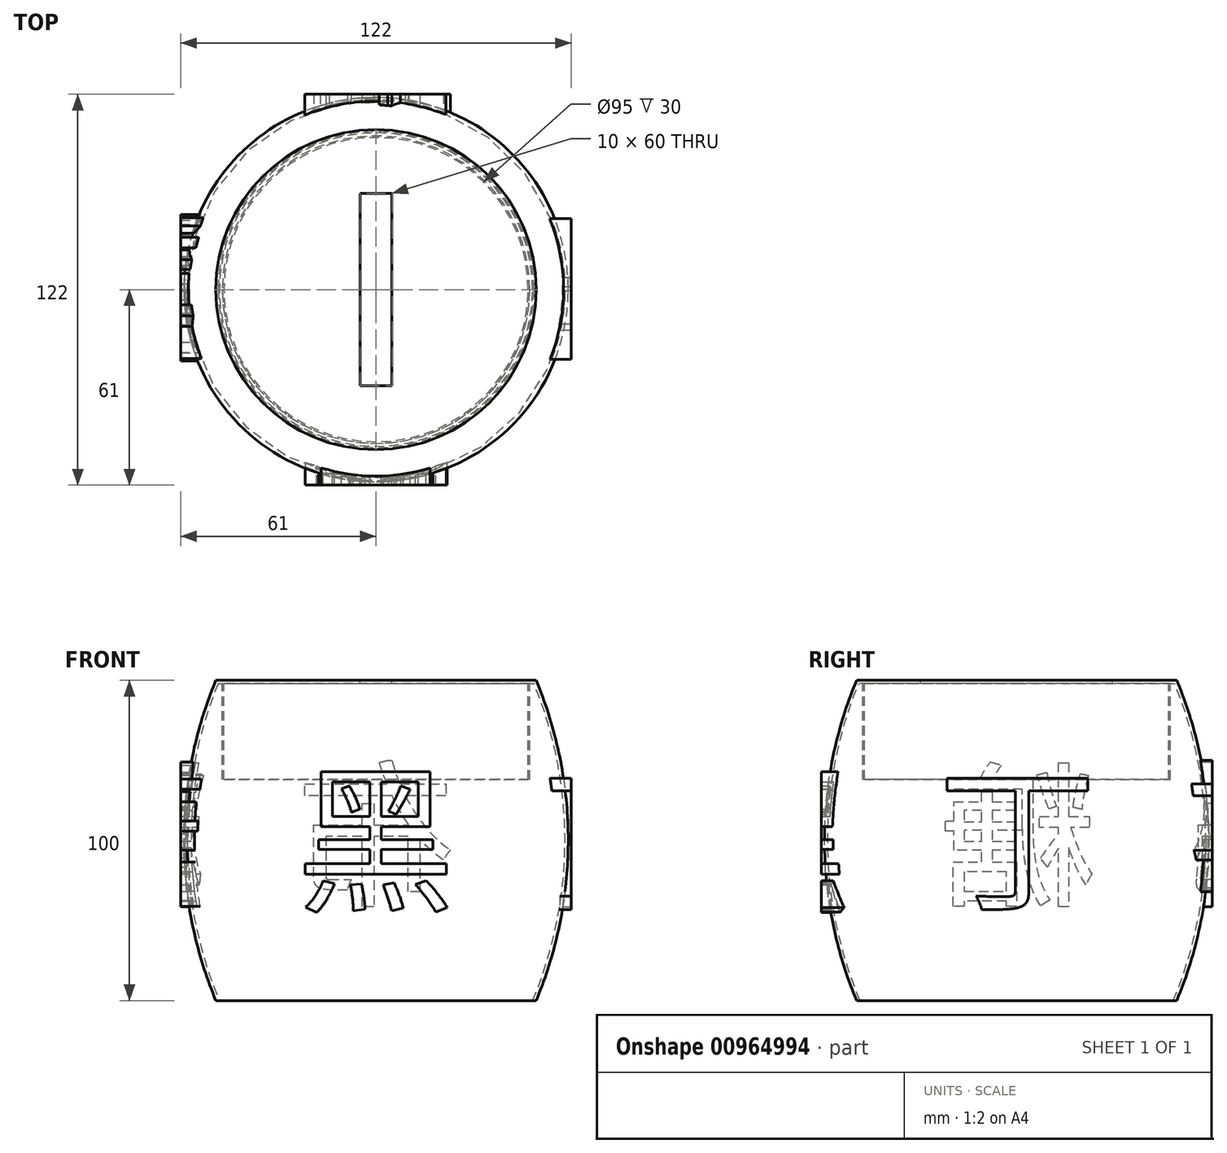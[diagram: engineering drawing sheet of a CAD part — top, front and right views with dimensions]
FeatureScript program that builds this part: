
annotation { "Feature Type Name" : "Feature", "Feature Type Description" : "" }
export const myFeature = defineFeature(function(context is Context, id is Id, definition is map)
    precondition{}
    {
        {
            var Q0;
            Q0=qCreatedBy(makeId("Front.planeOp"),FACE);
            var sketch = newSketch(context, id + "F0", { "sketchPlane" : qUnion([Q0])});
            skLineSegment(sketch, "E0.bottom", {"start": v(25, -25) * mm, "end": v(-25, -25) * mm});
            skLineSegment(sketch, "E0.top", {"start": v(25, 25) * mm, "end": v(-25, 25) * mm});
            skLineSegment(sketch, "E0.left", {"start": v(25, -25) * mm, "end": v(25, 25) * mm});
            skLineSegment(sketch, "E0.right", {"start": v(-25, -25) * mm, "end": v(-25, 25) * mm});
            skPoint(sketch, "E0.middle", {"position": v(0, 0) * mm});
            skText(sketch, "E1", { "text": "黑", "fontName": "NotoSansCJKsc-Regular.otf"});
            const initialGuessF0  = {"E1": [-0.025, -0.01845, 1, 0, 0.0359]};
            skSetInitialGuess(sketch, initialGuessF0);
            skSolve(sketch);
        }
        {
            var Q0;
            Q0=qCreatedBy(makeId("Right.planeOp"),FACE);
            var sketch = newSketch(context, id + "F1", { "sketchPlane" : qUnion([Q0])});
            skLineSegment(sketch, "E2.bottom", {"start": v(25, -25) * mm, "end": v(-25, -25) * mm});
            skLineSegment(sketch, "E2.top", {"start": v(25, 25) * mm, "end": v(-25, 25) * mm});
            skLineSegment(sketch, "E2.left", {"start": v(25, -25) * mm, "end": v(25, 25) * mm});
            skLineSegment(sketch, "E2.right", {"start": v(-25, -25) * mm, "end": v(-25, 25) * mm});
            skPoint(sketch, "E2.middle", {"position": v(0, 0) * mm});
            skText(sketch, "E3", { "text": "丁", "fontName": "NotoSansCJKsc-Regular.otf"});
            const initialGuessF1  = {"E3": [-0.025, -0.01819, 1, 0, 0.0363]};
            skSetInitialGuess(sketch, initialGuessF1);
            skSolve(sketch);
        }
        {
            var Q0;
            Q0=qCreatedBy(makeId("Right.planeOp"),FACE);
            var sketch = newSketch(context, id + "F2", { "sketchPlane" : qUnion([Q0])});
            skLineSegment(sketch, "E4.bottom", {"start": v(-25, -25) * mm, "end": v(25, -25) * mm});
            skLineSegment(sketch, "E4.top", {"start": v(-25, 25) * mm, "end": v(25, 25) * mm});
            skLineSegment(sketch, "E4.left", {"start": v(-25, -25) * mm, "end": v(-25, 25) * mm});
            skLineSegment(sketch, "E4.right", {"start": v(25, -25) * mm, "end": v(25, 25) * mm});
            skPoint(sketch, "E4.middle", {"position": v(0, 0) * mm});
            skSolve(sketch);
        }
        {
            var Q0;
            Q0 = qSketchRegion(id + "F2", true);
            extrude(context, id + "F3", {"entities" : qUnion([Q0]), "depth" : -1 * mm, "offsetDistance" : 25 * mm});
        }
        {
            var Q0;
            Q0=makeQuery(id+"F3.opExtrude","CAP_FACE",FACE,{"disambiguationData":[OSD([sQuery(id+"F2.wireOp",EDGE,"E4.bottom"),sQuery(id+"F2.wireOp",EDGE,"E4.top"),sQuery(id+"F2.wireOp",EDGE,"E4.left"),sQuery(id+"F2.wireOp",EDGE,"E4.right")])],"isStart":false});
            var sketch = newSketch(context, id + "F4", { "sketchPlane" : qUnion([Q0])});
            skText(sketch, "E5", { "text": "糖", "fontName": "NotoSansCJKsc-Regular.otf"});
            const initialGuessF4  = {"E5": [-0.025, -0.0169, 1, 0, 0.03547]};
            skSetInitialGuess(sketch, initialGuessF4);
            skSolve(sketch);
        }
        {
            var Q0;
            Q0=qCreatedBy(makeId("Front.planeOp"),FACE);
            var sketch = newSketch(context, id + "F5", { "sketchPlane" : qUnion([Q0])});
            skLineSegment(sketch, "E6.bottom", {"start": v(-25, -25) * mm, "end": v(25, -25) * mm});
            skLineSegment(sketch, "E6.top", {"start": v(-25, 25) * mm, "end": v(25, 25) * mm});
            skLineSegment(sketch, "E6.left", {"start": v(-25, -25) * mm, "end": v(-25, 25) * mm});
            skLineSegment(sketch, "E6.right", {"start": v(25, -25) * mm, "end": v(25, 25) * mm});
            skPoint(sketch, "E6.middle", {"position": v(0, 0) * mm});
            skSolve(sketch);
        }
        {
            var Q0;
            Q0=makeQuery(id+"F5.imprint","IMPRINT",FACE,{"disambiguationData":[TD([[makeQuery(id+"F5.imprint","IMPRINT",EDGE,{"derivedFrom":sQuery(id+"F5.wireOp",EDGE,"E6.bottom")}),1.0]])]});
            extrude(context, id + "F6", {"entities" : qUnion([Q0]), "depth" : -1 * mm, "offsetDistance" : 25 * mm});
        }
        {
            var Q0;
            Q0=makeQuery(id+"F6.opExtrude","CAP_FACE",FACE,{"disambiguationData":[OSD([sQuery(id+"F5.wireOp",EDGE,"E6.bottom"),sQuery(id+"F5.wireOp",EDGE,"E6.top"),sQuery(id+"F5.wireOp",EDGE,"E6.left"),sQuery(id+"F5.wireOp",EDGE,"E6.right")])],"isStart":false});
            var sketch = newSketch(context, id + "F7", { "sketchPlane" : qUnion([Q0])});
            skText(sketch, "E7", { "text": "布", "fontName": "NotoSansCJKsc-Regular.otf"});
            const initialGuessF7  = {"E7": [-0.025, -0.01683, 1, 0, 0.03622]};
            skSetInitialGuess(sketch, initialGuessF7);
            skSolve(sketch);
        }
        {
            var Q0;
            Q0=makeQuery(id+"F7.imprint","IMPRINT",FACE,{"disambiguationData":[TD([[makeQuery(id+"F7.imprint","IMPRINT",EDGE,{"derivedFrom":sQuery(id+"F7.wireOp",EDGE,"E7.sketch_text.stroke-0")}),1.0]])]});
            extrude(context, id + "F8", {"entities" : qUnion([Q0]), "operationType" : NewBodyOperationType.ADD, "depth" : 60 * mm, "offsetDistance" : 25 * mm});
        }
        {
            var Q0;
            Q0=makeQuery(id+"F4.imprint","IMPRINT",FACE,{"disambiguationData":[TD([[makeQuery(id+"F4.imprint","IMPRINT",EDGE,{"derivedFrom":sQuery(id+"F4.wireOp",EDGE,"E5.sketch_text.stroke-39")}),1.0]])]});
            var Q1;
            Q1=makeQuery(id+"F4.imprint","IMPRINT",FACE,{"disambiguationData":[TD([[makeQuery(id+"F4.imprint","IMPRINT",EDGE,{"derivedFrom":sQuery(id+"F4.wireOp",EDGE,"E5.sketch_text.stroke-27")}),1.0]])]});
            var Q2;
            Q2=makeQuery(id+"F4.imprint","IMPRINT",FACE,{"disambiguationData":[TD([[makeQuery(id+"F4.imprint","IMPRINT",EDGE,{"derivedFrom":sQuery(id+"F4.wireOp",EDGE,"E5.sketch_text.stroke-0")}),1.0]])]});
            var Q3;
            Q3=makeQuery(id+"F4.imprint","IMPRINT",FACE,{"disambiguationData":[TD([[makeQuery(id+"F4.imprint","IMPRINT",EDGE,{"derivedFrom":sQuery(id+"F4.wireOp",EDGE,"E5.sketch_text.stroke-4")}),1.0]])]});
            var Q4;
            Q4=makeQuery(id+"F4.imprint","IMPRINT",FACE,{"disambiguationData":[TD([[makeQuery(id+"F4.imprint","IMPRINT",EDGE,{"derivedFrom":sQuery(id+"F4.wireOp",EDGE,"E5.sketch_text.stroke-8")}),1.0]])]});
            extrude(context, id + "F9", {"entities" : qUnion([Q0, Q1, Q2, Q3, Q4]), "operationType" : NewBodyOperationType.ADD, "depth" : 60 * mm, "offsetDistance" : 25 * mm});
        }
        {
            var Q0;
            Q0=makeQuery(id+"F0.imprint","IMPRINT",FACE,{"disambiguationData":[TD([[makeQuery(id+"F0.imprint","IMPRINT",EDGE,{"derivedFrom":sQuery(id+"F0.wireOp",EDGE,"E1.sketch_text.stroke-8")}),1.0]])]});
            var Q1;
            Q1=makeQuery(id+"F0.imprint","IMPRINT",FACE,{"disambiguationData":[TD([[makeQuery(id+"F0.imprint","IMPRINT",EDGE,{"derivedFrom":sQuery(id+"F0.wireOp",EDGE,"E1.sketch_text.stroke-4")}),1.0]])]});
            var Q2;
            Q2=makeQuery(id+"F0.imprint","IMPRINT",FACE,{"disambiguationData":[TD([[makeQuery(id+"F0.imprint","IMPRINT",EDGE,{"derivedFrom":sQuery(id+"F0.wireOp",EDGE,"E1.sketch_text.stroke-0")}),1.0]])]});
            var Q3;
            Q3=makeQuery(id+"F0.imprint","IMPRINT",FACE,{"disambiguationData":[TD([[makeQuery(id+"F0.imprint","IMPRINT",EDGE,{"derivedFrom":sQuery(id+"F0.wireOp",EDGE,"E1.sketch_text.stroke-48")}),1.0]])]});
            var Q4;
            Q4=makeQuery(id+"F0.imprint","IMPRINT",FACE,{"disambiguationData":[TD([[makeQuery(id+"F0.imprint","IMPRINT",EDGE,{"derivedFrom":sQuery(id+"F0.wireOp",EDGE,"E1.sketch_text.stroke-44")}),1.0]])]});
            var Q5;
            Q5=makeQuery(id+"F0.imprint","IMPRINT",FACE,{"disambiguationData":[TD([[makeQuery(id+"F0.imprint","IMPRINT",EDGE,{"derivedFrom":sQuery(id+"F0.wireOp",EDGE,"E1.sketch_text.stroke-40")}),1.0]])]});
            var Q6;
            Q6=makeQuery(id+"F0.imprint","IMPRINT",FACE,{"disambiguationData":[TD([[makeQuery(id+"F0.imprint","IMPRINT",EDGE,{"derivedFrom":sQuery(id+"F0.wireOp",EDGE,"E1.sketch_text.stroke-36")}),1.0]])]});
            extrude(context, id + "F10", {"entities" : qUnion([Q0, Q1, Q2, Q3, Q4, Q5, Q6]), "depth" : 61 * mm, "offsetDistance" : 25 * mm});
        }
        {
            var Q0;
            Q0=makeQuery(id+"F1.imprint","IMPRINT",FACE,{"disambiguationData":[TD([[makeQuery(id+"F1.imprint","IMPRINT",EDGE,{"derivedFrom":sQuery(id+"F1.wireOp",EDGE,"E3.sketch_text.stroke-0")}),1.0]])]});
            extrude(context, id + "F11", {"entities" : qUnion([Q0]), "depth" : 61 * mm, "offsetDistance" : 25 * mm});
        }
        {
            var Q0;
            Q0=qCreatedBy(makeId("Right.planeOp"),FACE);
            var sketch = newSketch(context, id + "F12", { "sketchPlane" : qUnion([Q0])});
            skLineSegment(sketch, "E8", {"start": v(0, 0) * mm, "end": v(0, 50) * mm, "construction": true});
            skLineSegment(sketch, "E9", {"start": v(0, 0) * mm, "end": v(0, -50) * mm, "construction": true});
            skLineSegment(sketch, "E10", {"start": v(0, 50) * mm, "end": v(50, 50) * mm, "construction": true});
            skLineSegment(sketch, "E11", {"start": v(0, 0) * mm, "end": v(60, 0) * mm, "construction": true});
            skLineSegment(sketch, "E12", {"start": v(0, -50) * mm, "end": v(50, -50) * mm, "construction": true});
            skLineSegment(sketch, "E13", {"start": v(0, 50) * mm, "end": v(0, -50) * mm});
            skLineSegment(sketch, "E14", {"start": v(50, -50) * mm, "end": v(0, -50) * mm});
            skLineSegment(sketch, "E15", {"start": v(50, 50) * mm, "end": v(0, 50) * mm});
            skArc(sketch, "E16", {"start": v(50, -50) * mm, "mid": v(60, 0) * mm, "end": v(50, 50) * mm});
            skSolve(sketch);
        }
        {
            var Q0;
            Q0=qCreatedBy(makeId("Top.planeOp"),FACE);
            var sketch = newSketch(context, id + "F13", { "sketchPlane" : qUnion([Q0])});
            skCircle(sketch, "E17", {"center": v(0, 0) * mm, "radius": 5 * mm});
            skSolve(sketch);
        }
        {
            var Q0;
            Q0=makeQuery(id+"F12.imprint","IMPRINT",FACE,{"disambiguationData":[TD([[makeQuery(id+"F12.imprint","IMPRINT",EDGE,{"derivedFrom":sQuery(id+"F12.wireOp",EDGE,"E13")}),1.0]])]});
            var Q1;
            Q1=sQuery(id+"F13.wireOp",EDGE,"E17");
            sweep(context, id + "F14", {"operationType" : NewBodyOperationType.REMOVE, "profiles" : qUnion([Q0]), "path" : qUnion([Q1])});
        }
        {
            var Q0;
            Q0=qCreatedBy(makeId("Front.planeOp"),FACE);
            var sketch = newSketch(context, id + "F15", { "sketchPlane" : qUnion([Q0])});
            skLineSegment(sketch, "E18", {"start": v(0, 0) * mm, "end": v(0, 50) * mm, "construction": true});
            skLineSegment(sketch, "E19", {"start": v(0, 0) * mm, "end": v(0, -50) * mm, "construction": true});
            skLineSegment(sketch, "E20", {"start": v(0, -50) * mm, "end": v(50, -50) * mm, "construction": true});
            skLineSegment(sketch, "E21", {"start": v(0, 50) * mm, "end": v(50, 50) * mm, "construction": true});
            skLineSegment(sketch, "E22", {"start": v(0, 0) * mm, "end": v(60, 0) * mm, "construction": true});
            skLineSegment(sketch, "E23", {"start": v(0, 50) * mm, "end": v(0, -50) * mm});
            skLineSegment(sketch, "E24", {"start": v(50, -50) * mm, "end": v(0, -50) * mm});
            skLineSegment(sketch, "E25", {"start": v(0, 50) * mm, "end": v(50, 50) * mm});
            skArc(sketch, "E26", {"start": v(50, -50) * mm, "mid": v(60, 0) * mm, "end": v(50, 50) * mm});
            skSolve(sketch);
        }
        {
            var Q0;
            Q0=qCreatedBy(makeId("Top.planeOp"),FACE);
            var sketch = newSketch(context, id + "F16", { "sketchPlane" : qUnion([Q0])});
            skCircle(sketch, "E27", {"center": v(0, 0) * mm, "radius": 5 * mm});
            skSolve(sketch);
        }
        {
            var Q0;
            Q0=makeQuery(id+"F15.imprint","IMPRINT",FACE,{"disambiguationData":[TD([[makeQuery(id+"F15.imprint","IMPRINT",EDGE,{"derivedFrom":sQuery(id+"F15.wireOp",EDGE,"E23")}),1.0]])]});
            var Q1;
            Q1=sQuery(id+"F16.wireOp",EDGE,"E27");
            sweep(context, id + "F17", {"profiles" : qUnion([Q0]), "path" : qUnion([Q1])});
        }
        {
            var Q0;
            Q0=makeQuery(id+"F17.opSweep","SWEPT_FACE",FACE,{"disambiguationData":[OSD([sQuery(id+"F15.wireOp",EDGE,"E24"),sQuery(id+"F16.wireOp",EDGE,"E27")])]});
            shell(context, id + "F18", {"entities" : qUnion([Q0]), "thickness" : 1 * mm});
        }
        {
            var Q0;
            Q0=makeQuery(id+"F17.opSweep","SWEPT_FACE",FACE,{"disambiguationData":[OSD([sQuery(id+"F15.wireOp",EDGE,"E25"),sQuery(id+"F16.wireOp",EDGE,"E27")])]});
            var sketch = newSketch(context, id + "F19", { "sketchPlane" : qUnion([Q0])});
            skLineSegment(sketch, "E28.bottom", {"start": v(5, -30) * mm, "end": v(-5, -30) * mm});
            skLineSegment(sketch, "E28.top", {"start": v(5, 30) * mm, "end": v(-5, 30) * mm});
            skLineSegment(sketch, "E28.left", {"start": v(5, -30) * mm, "end": v(5, 30) * mm});
            skLineSegment(sketch, "E28.right", {"start": v(-5, -30) * mm, "end": v(-5, 30) * mm});
            skPoint(sketch, "E28.middle", {"position": v(0, 0) * mm});
            skSolve(sketch);
        }
        {
            var Q0;
            Q0=qCreatedBy(makeId("Front.planeOp"),FACE);
            var sketch = newSketch(context, id + "F20", { "sketchPlane" : qUnion([Q0])});
            skLineSegment(sketch, "E29", {"start": v(0, 54.82) * mm, "end": v(0, 22.75) * mm});
            skSolve(sketch);
        }
        {
            var Q0;
            Q0=makeQuery(id+"F19.imprint","IMPRINT",FACE,{"disambiguationData":[TD([[makeQuery(id+"F19.imprint","IMPRINT",EDGE,{"derivedFrom":sQuery(id+"F19.wireOp",EDGE,"E28.bottom")}),-1.0]])]});
            var Q1;
            Q1=sQuery(id+"F20.wireOp",EDGE,"E29");
            sweep(context, id + "F21", {"operationType" : NewBodyOperationType.REMOVE, "profiles" : qUnion([Q0]), "path" : qUnion([Q1])});
        }
        {
            var Q0;
            Q0=makeQuery(id+"F18.opShell","OFFSET_FACE",FACE,{"disambiguationData":[OSD([sQuery(id+"F15.wireOp",EDGE,"E25"),sQuery(id+"F16.wireOp",EDGE,"E27")])]});
            var sketch = newSketch(context, id + "F22", { "sketchPlane" : qUnion([Q0])});
            skCircle(sketch, "E30", {"center": v(0, 0) * mm, "radius": 47.5 * mm});
            skCircle(sketch, "E31", {"center": v(0, 0) * mm, "radius": 48 * mm});
            skSolve(sketch);
        }
        {
            var Q0;
            Q0=makeQuery(id+"F22.imprint","IMPRINT",FACE,{"disambiguationData":[TD([[makeQuery(id+"F22.imprint","IMPRINT",EDGE,{"derivedFrom":sQuery(id+"F22.wireOp",EDGE,"E30")}),-1.0]])]});
            extrude(context, id + "F23", {"entities" : qUnion([Q0]), "operationType" : NewBodyOperationType.ADD, "depth" : 30 * mm, "offsetDistance" : 25 * mm});
        }
    });
